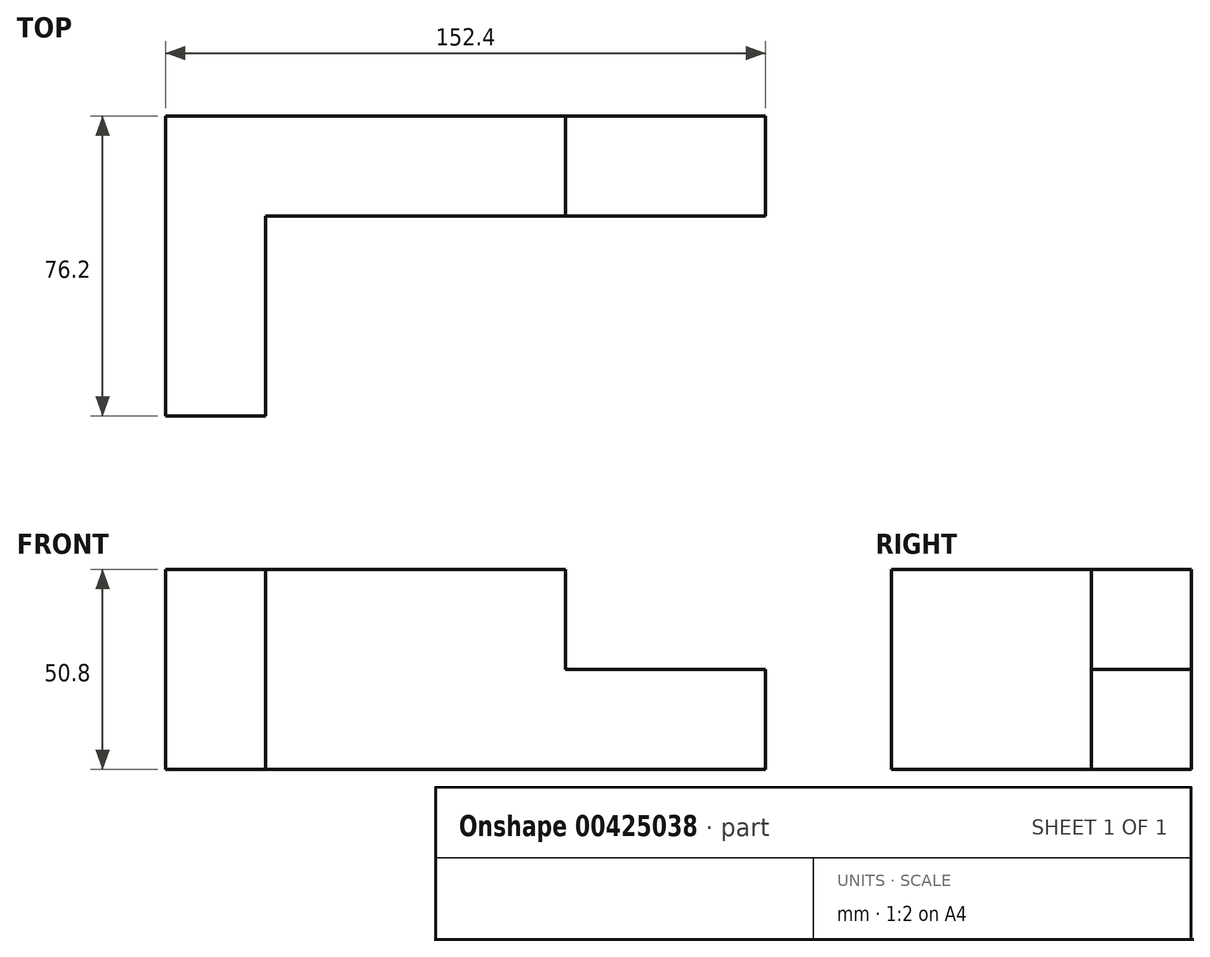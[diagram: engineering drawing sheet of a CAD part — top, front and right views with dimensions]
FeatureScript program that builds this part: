
annotation { "Feature Type Name" : "Feature", "Feature Type Description" : "" }
export const myFeature = defineFeature(function(context is Context, id is Id, definition is map)
    precondition{}
    {
        {
            var Q0;
            Q0=qCreatedBy(makeId("Front.planeOp"),FACE);
            var sketch = newSketch(context, id + "F0", { "sketchPlane" : qUnion([Q0])});
            skLineSegment(sketch, "E0", {"start": v(0, 0) * mm, "end": v(152.4, 0) * mm});
            skLineSegment(sketch, "E1", {"start": v(152.4, 0) * mm, "end": v(152.4, 50.8) * mm});
            skLineSegment(sketch, "E2", {"start": v(152.4, 50.8) * mm, "end": v(0, 50.8) * mm});
            skLineSegment(sketch, "E3", {"start": v(0, 50.8) * mm, "end": v(0, 0) * mm});
            skSolve(sketch);
        }
        {
            var Q0;
            Q0=makeQuery(id+"F0.imprint","IMPRINT",FACE,{"disambiguationData":[TD([[makeQuery(id+"F0.imprint","IMPRINT",EDGE,{"derivedFrom":sQuery(id+"F0.wireOp",EDGE,"E0")}),1.0]])]});
            extrude(context, id + "F1", {"entities" : qUnion([Q0]), "depth" : 76.2 * mm});
        }
        {
            var Q0;
            Q0=makeQuery(id+"F1.opExtrude","CAP_FACE",FACE,{"disambiguationData":[OSD([sQuery(id+"F0.wireOp",EDGE,"E0"),sQuery(id+"F0.wireOp",EDGE,"E1"),sQuery(id+"F0.wireOp",EDGE,"E2"),sQuery(id+"F0.wireOp",EDGE,"E3")])],"isStart":false});
            var sketch = newSketch(context, id + "F2", { "sketchPlane" : qUnion([Q0])});
            skLineSegment(sketch, "E4", {"start": v(152.4, 0) * mm, "end": v(25.4, 0) * mm});
            skLineSegment(sketch, "E5", {"start": v(25.4, 0) * mm, "end": v(25.4, 50.8) * mm});
            skLineSegment(sketch, "E6", {"start": v(25.4, 50.8) * mm, "end": v(152.4, 50.8) * mm});
            skLineSegment(sketch, "E7", {"start": v(152.4, 50.8) * mm, "end": v(152.4, 0) * mm});
            skSolve(sketch);
        }
        {
            var Q0;
            Q0=makeQuery(id+"F2.imprint","IMPRINT",FACE,{"disambiguationData":[TD([[makeQuery(id+"F2.imprint","IMPRINT",EDGE,{"derivedFrom":sQuery(id+"F2.wireOp",EDGE,"E4")}),1.0]])]});
            extrude(context, id + "F3", {"entities" : qUnion([Q0]), "operationType" : NewBodyOperationType.REMOVE, "oppositeDirection" : true, "depth" : 50.8 * mm});
        }
        {
            var Q0;
            Q0=makeQuery(id+"F3.boolean.opBoolean","COPY",FACE,{"derivedFrom":makeQuery(id+"F3.opExtrude","CAP_FACE",FACE,{"disambiguationData":[OSD([sQuery(id+"F2.wireOp",EDGE,"E4"),sQuery(id+"F2.wireOp",EDGE,"E5"),sQuery(id+"F2.wireOp",EDGE,"E6"),sQuery(id+"F2.wireOp",EDGE,"E7")])],"isStart":false})});
            var sketch = newSketch(context, id + "F4", { "sketchPlane" : qUnion([Q0])});
            skLineSegment(sketch, "E8", {"start": v(152.4, 50.8) * mm, "end": v(101.6, 50.8) * mm});
            skLineSegment(sketch, "E9", {"start": v(101.6, 50.8) * mm, "end": v(101.6, 25.4) * mm});
            skLineSegment(sketch, "E10", {"start": v(101.6, 25.4) * mm, "end": v(152.4, 25.4) * mm});
            skLineSegment(sketch, "E11", {"start": v(152.4, 25.4) * mm, "end": v(152.4, 50.8) * mm});
            skSolve(sketch);
        }
        {
            var Q0;
            Q0=makeQuery(id+"F4.imprint","IMPRINT",FACE,{"disambiguationData":[TD([[makeQuery(id+"F4.imprint","IMPRINT",EDGE,{"derivedFrom":sQuery(id+"F4.wireOp",EDGE,"E8")}),1.0]])]});
            extrude(context, id + "F5", {"entities" : qUnion([Q0]), "operationType" : NewBodyOperationType.REMOVE, "oppositeDirection" : true, "depth" : 25.4 * mm});
        }
    });
